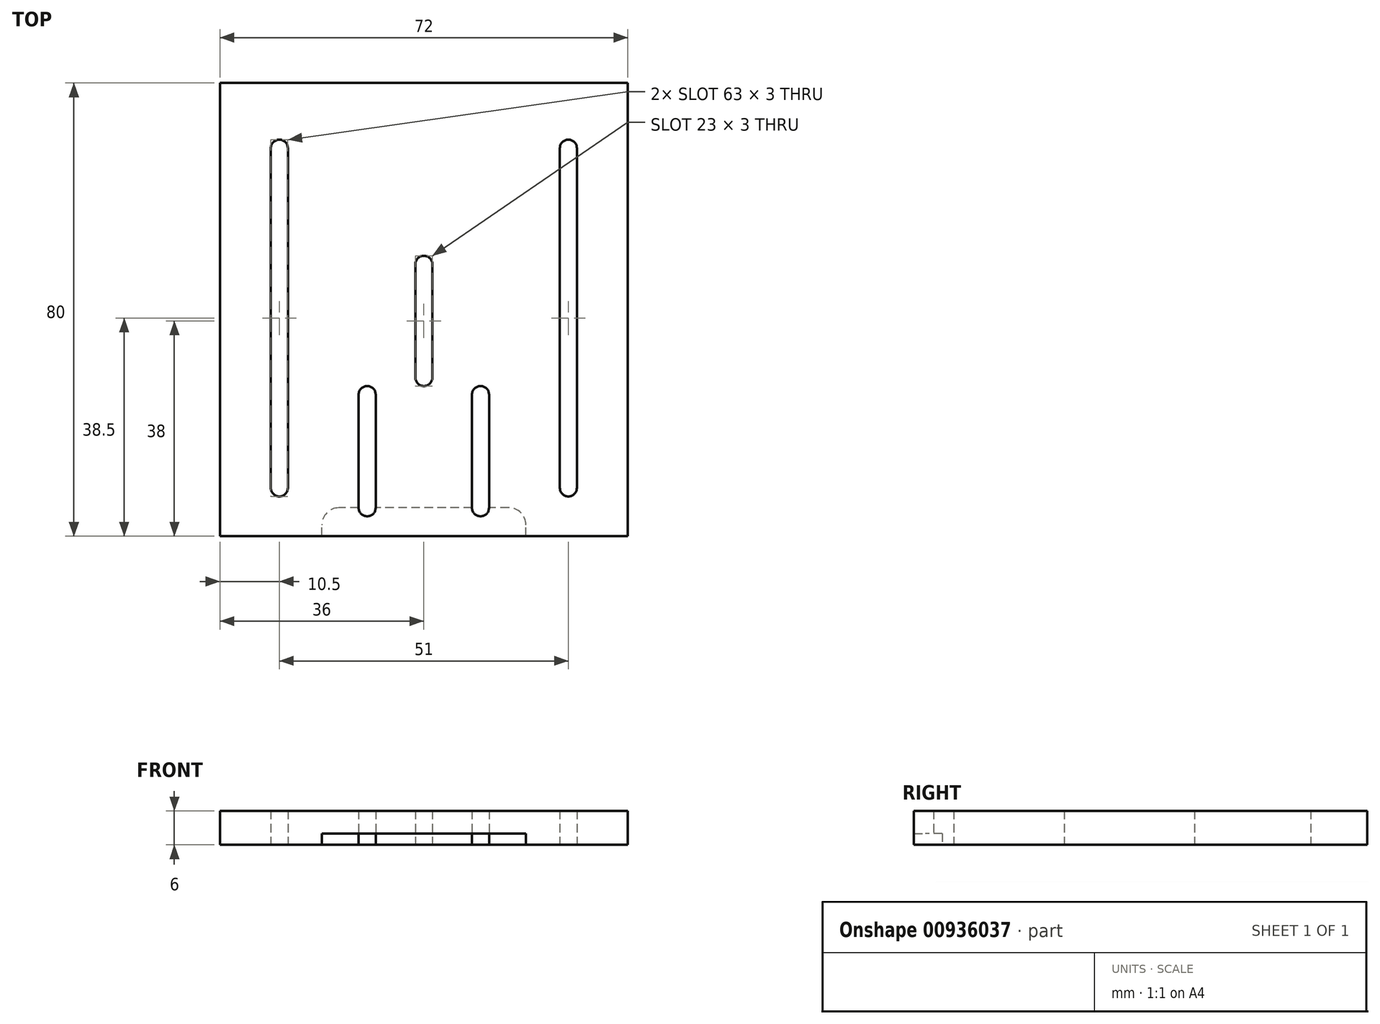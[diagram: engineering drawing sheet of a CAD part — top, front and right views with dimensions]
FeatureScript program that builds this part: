
annotation { "Feature Type Name" : "Feature", "Feature Type Description" : "" }
export const myFeature = defineFeature(function(context is Context, id is Id, definition is map)
    precondition{}
    {
        {
            var Q0;
            Q0=qCreatedBy(makeId("Top.planeOp"),FACE);
            var sketch = newSketch(context, id + "F0", { "sketchPlane" : qUnion([Q0])});
            skLineSegment(sketch, "E0.bottom", {"start": v(36, -40) * mm, "end": v(-36, -40) * mm});
            skLineSegment(sketch, "E0.top", {"start": v(36, 40) * mm, "end": v(-36, 40) * mm});
            skLineSegment(sketch, "E0.left", {"start": v(36, -40) * mm, "end": v(36, 40) * mm});
            skLineSegment(sketch, "E0.right", {"start": v(-36, -40) * mm, "end": v(-36, 40) * mm});
            skPoint(sketch, "E0.middle", {"position": v(0, 0) * mm});
            skLineSegment(sketch, "E1", {"start": v(27, 28.5) * mm, "end": v(27, -31.5) * mm});
            skLineSegment(sketch, "E2", {"start": v(24, -31.5) * mm, "end": v(24, 28.5) * mm});
            skLineSegment(sketch, "E3", {"start": v(-24, -31.5) * mm, "end": v(-24, 28.5) * mm});
            skLineSegment(sketch, "E4", {"start": v(-27, 28.5) * mm, "end": v(-27, -31.5) * mm});
            skArc(sketch, "E5", {"start": v(-27, 28.5) * mm, "mid": v(-25.5, 30) * mm, "end": v(-24, 28.5) * mm});
            skArc(sketch, "E6", {"start": v(24, 28.5) * mm, "mid": v(25.5, 30) * mm, "end": v(27, 28.5) * mm});
            skArc(sketch, "E7", {"start": v(-27, -31.5) * mm, "mid": v(-25.5, -33) * mm, "end": v(-24, -31.5) * mm});
            skArc(sketch, "E8", {"start": v(24, -31.5) * mm, "mid": v(25.5, -33) * mm, "end": v(27, -31.5) * mm});
            skLineSegment(sketch, "E9", {"start": v(-11.5, -35) * mm, "end": v(-11.5, -15) * mm});
            skLineSegment(sketch, "E10", {"start": v(-11.5, -15) * mm, "end": v(-8.5, -15) * mm});
            skLineSegment(sketch, "E11", {"start": v(-8.5, -15) * mm, "end": v(-8.5, -35) * mm});
            skLineSegment(sketch, "E12", {"start": v(-8.5, -35) * mm, "end": v(-11.5, -35) * mm});
            skLineSegment(sketch, "E13", {"start": v(8.5, -35) * mm, "end": v(8.5, -15) * mm});
            skLineSegment(sketch, "E14", {"start": v(8.5, -15) * mm, "end": v(11.5, -15) * mm});
            skLineSegment(sketch, "E15", {"start": v(11.5, -15) * mm, "end": v(11.5, -35) * mm});
            skLineSegment(sketch, "E16", {"start": v(11.5, -35) * mm, "end": v(8.5, -35) * mm});
            skLineSegment(sketch, "E17", {"start": v(-1.5, 8) * mm, "end": v(1.5, 8) * mm});
            skLineSegment(sketch, "E18", {"start": v(1.5, 8) * mm, "end": v(1.5, -12) * mm});
            skLineSegment(sketch, "E19", {"start": v(1.5, -12) * mm, "end": v(-1.5, -12) * mm});
            skLineSegment(sketch, "E20", {"start": v(-1.5, -12) * mm, "end": v(-1.5, 8) * mm});
            skArc(sketch, "E21", {"start": v(-8.5, -35) * mm, "mid": v(-10, -36.5) * mm, "end": v(-11.5, -35) * mm});
            skArc(sketch, "E22", {"start": v(-8.5, -15) * mm, "mid": v(-10, -13.5) * mm, "end": v(-11.5, -15) * mm});
            skArc(sketch, "E23", {"start": v(-1.5, -12) * mm, "mid": v(0, -13.5) * mm, "end": v(1.5, -12) * mm});
            skArc(sketch, "E24", {"start": v(11.5, -15) * mm, "mid": v(10, -13.5) * mm, "end": v(8.5, -15) * mm});
            skArc(sketch, "E25", {"start": v(11.5, -35) * mm, "mid": v(10, -36.5) * mm, "end": v(8.5, -35) * mm});
            skArc(sketch, "E26", {"start": v(1.5, 8) * mm, "mid": v(0, 9.5) * mm, "end": v(-1.5, 8) * mm});
            skSolve(sketch);
        }
        {
            var Q0;
            Q0 = qSketchRegion(id + "F0", true);
            extrude(context, id + "F1", {"entities" : qUnion([Q0]), "depth" : 6 * mm, "offsetDistance" : 25 * mm});
        }
        {
            var Q0;
            Q0 = qSketchRegion(id + "F0", true);
            extrude(context, id + "F2", {"entities" : qUnion([Q0]), "operationType" : NewBodyOperationType.REMOVE, "oppositeDirection" : true, "depth" : 6 * mm, "offsetDistance" : 25 * mm});
        }
        {
            var Q0;
            Q0=makeQuery(id+"F1.opExtrude","CAP_FACE",FACE,{"disambiguationData":[OSD([sQuery(id+"F0.wireOp",EDGE,"E0.bottom"),sQuery(id+"F0.wireOp",EDGE,"E0.top"),sQuery(id+"F0.wireOp",EDGE,"E0.left"),sQuery(id+"F0.wireOp",EDGE,"E0.right"),sQuery(id+"F0.wireOp",EDGE,"E1"),sQuery(id+"F0.wireOp",EDGE,"E2"),sQuery(id+"F0.wireOp",EDGE,"E3"),sQuery(id+"F0.wireOp",EDGE,"E4"),sQuery(id+"F0.wireOp",EDGE,"E5"),sQuery(id+"F0.wireOp",EDGE,"E6"),sQuery(id+"F0.wireOp",EDGE,"E7"),sQuery(id+"F0.wireOp",EDGE,"E8"),sQuery(id+"F0.wireOp",EDGE,"E9"),sQuery(id+"F0.wireOp",EDGE,"E11"),sQuery(id+"F0.wireOp",EDGE,"E13"),sQuery(id+"F0.wireOp",EDGE,"E15"),sQuery(id+"F0.wireOp",EDGE,"E18"),sQuery(id+"F0.wireOp",EDGE,"E20"),sQuery(id+"F0.wireOp",EDGE,"E21"),sQuery(id+"F0.wireOp",EDGE,"E22"),sQuery(id+"F0.wireOp",EDGE,"E23"),sQuery(id+"F0.wireOp",EDGE,"E24"),sQuery(id+"F0.wireOp",EDGE,"E25"),sQuery(id+"F0.wireOp",EDGE,"E26")])],"isStart":true});
            var sketch = newSketch(context, id + "F3", { "sketchPlane" : qUnion([Q0])});
            skLineSegment(sketch, "E27.bottom", {"start": v(18, 40) * mm, "end": v(-18, 40) * mm});
            skLineSegment(sketch, "E27.top", {"start": v(18, 35) * mm, "end": v(-18, 35) * mm});
            skLineSegment(sketch, "E27.left", {"start": v(18, 40) * mm, "end": v(18, 35) * mm});
            skLineSegment(sketch, "E27.right", {"start": v(-18, 40) * mm, "end": v(-18, 35) * mm});
            skPoint(sketch, "E27.middle", {"position": v(0, 37.5) * mm});
            skSolve(sketch);
        }
        {
            var Q0;
            Q0=makeQuery(id+"F3.imprint","IMPRINT",FACE,{"disambiguationData":[TD([[makeQuery(id+"F3.imprint","IMPRINT",EDGE,{"derivedFrom":sQuery(id+"F3.wireOp",EDGE,"E27.bottom")}),1.0]])]});
            extrude(context, id + "F4", {"entities" : qUnion([Q0]), "operationType" : NewBodyOperationType.REMOVE, "oppositeDirection" : true, "depth" : 2 * mm, "offsetDistance" : 25 * mm});
        }
        {
            var Q0;
            Q0=makeQuery(id+"F4.boolean.opBoolean","COPY",EDGE,{"derivedFrom":makeQuery(id+"F4.opExtrude","SWEPT_EDGE",EDGE,{"disambiguationData":[OSD([sQuery(id+"F3.wireOp",EDGE,"E27.top"),sQuery(id+"F3.wireOp",EDGE,"E27.right")])]})});
            var Q1;
            Q1=makeQuery(id+"F4.boolean.opBoolean","COPY",EDGE,{"derivedFrom":makeQuery(id+"F4.opExtrude","SWEPT_EDGE",EDGE,{"disambiguationData":[OSD([sQuery(id+"F3.wireOp",EDGE,"E27.top"),sQuery(id+"F3.wireOp",EDGE,"E27.left")])]})});
            fillet(context, id + "F5", {"entities" : qUnion([Q0, Q1]), "tangentPropagation" : true, "radius" : 3 * mm, "defaultsChanged" : true, "vertexSettings" : [], "allowEdgeOverflow" : false});
        }
    });
